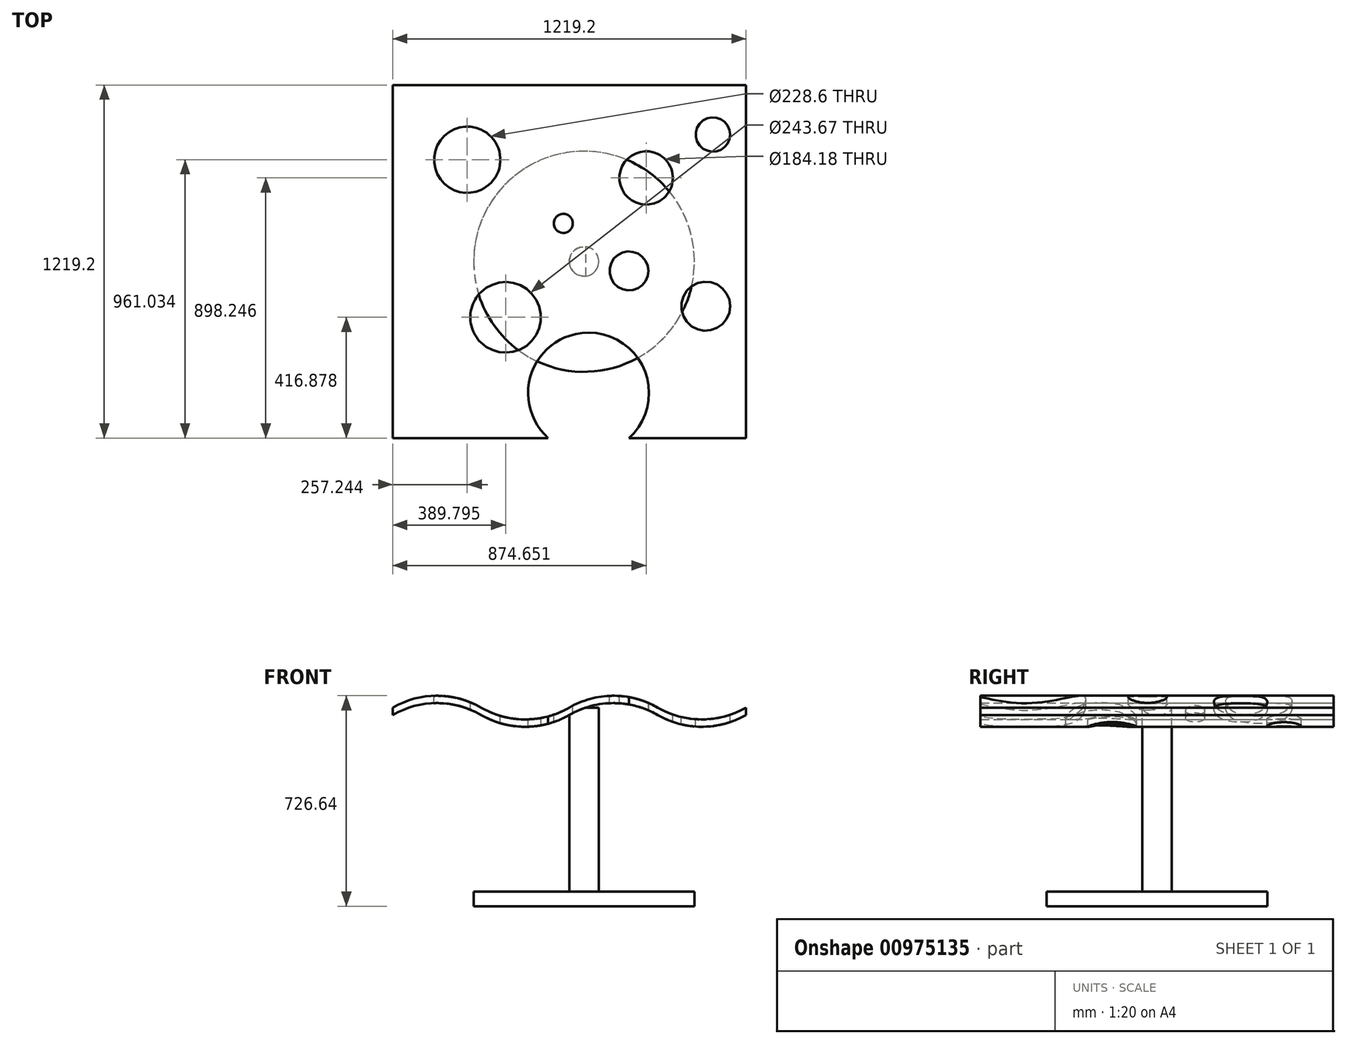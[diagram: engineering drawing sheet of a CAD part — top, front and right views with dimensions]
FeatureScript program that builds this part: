
annotation { "Feature Type Name" : "Feature", "Feature Type Description" : "" }
export const myFeature = defineFeature(function(context is Context, id is Id, definition is map)
    precondition{}
    {
        {
            var Q0;
            Q0=qCreatedBy(makeId("Front.planeOp"),FACE);
            var sketch = newSketch(context, id + "F0", { "sketchPlane" : qUnion([Q0])});
            skArc(sketch, "E0", {"start": v(-355.6, 0) * mm, "mid": v(-508, 40.84) * mm, "end": v(-660.4, 0) * mm});
            skArc(sketch, "E1", {"start": v(-355.6, 0) * mm, "mid": v(-203.2, -40.84) * mm, "end": v(-50.8, 0) * mm});
            skArc(sketch, "E2", {"start": v(254, 0) * mm, "mid": v(101.6, 40.84) * mm, "end": v(-50.8, 0) * mm});
            skArc(sketch, "E3", {"start": v(254, 0) * mm, "mid": v(406.4, -40.84) * mm, "end": v(558.8, 0) * mm});
            skLineSegment(sketch, "E4", {"start": v(-660.4, 0) * mm, "end": v(-660.4, -25.4) * mm});
            skLineSegment(sketch, "E5", {"start": v(-355.6, 0) * mm, "end": v(-355.6, -25.4) * mm});
            skLineSegment(sketch, "E6", {"start": v(-50.8, 0) * mm, "end": v(-50.8, -25.4) * mm});
            skLineSegment(sketch, "E7", {"start": v(254, 0) * mm, "end": v(254, -25.4) * mm});
            skLineSegment(sketch, "E8", {"start": v(558.8, 0) * mm, "end": v(558.8, -25.4) * mm});
            skArc(sketch, "E9", {"start": v(-355.6, -25.4) * mm, "mid": v(-508, 15.44) * mm, "end": v(-660.4, -25.4) * mm});
            skArc(sketch, "E10", {"start": v(-355.6, -25.4) * mm, "mid": v(-203.2, -66.24) * mm, "end": v(-50.8, -25.4) * mm});
            skArc(sketch, "E11", {"start": v(254, -25.4) * mm, "mid": v(101.6, 15.44) * mm, "end": v(-50.8, -25.4) * mm});
            skArc(sketch, "E12", {"start": v(254, -25.4) * mm, "mid": v(406.4, -66.24) * mm, "end": v(558.8, -25.4) * mm});
            skSolve(sketch);
        }
        {
            var Q0;
            Q0=makeQuery(id+"F0.imprint","IMPRINT",FACE,{"disambiguationData":[TD([[makeQuery(id+"F0.imprint","IMPRINT",EDGE,{"derivedFrom":sQuery(id+"F0.wireOp",EDGE,"E0")}),1.0]])]});
            var Q1;
            Q1=makeQuery(id+"F0.imprint","IMPRINT",FACE,{"disambiguationData":[TD([[makeQuery(id+"F0.imprint","IMPRINT",EDGE,{"derivedFrom":sQuery(id+"F0.wireOp",EDGE,"E1")}),-1.0]])]});
            var Q2;
            Q2=makeQuery(id+"F0.imprint","IMPRINT",FACE,{"disambiguationData":[TD([[makeQuery(id+"F0.imprint","IMPRINT",EDGE,{"derivedFrom":sQuery(id+"F0.wireOp",EDGE,"E2")}),1.0]])]});
            var Q3;
            Q3=makeQuery(id+"F0.imprint","IMPRINT",FACE,{"disambiguationData":[TD([[makeQuery(id+"F0.imprint","IMPRINT",EDGE,{"derivedFrom":sQuery(id+"F0.wireOp",EDGE,"E3")}),-1.0]])]});
            extrude(context, id + "F1", {"entities" : qUnion([Q0, Q1, Q2, Q3]), "endBound" : BoundingType.SYMMETRIC, "depth" : 1219.2 * mm, "offsetDistance" : 25.4 * mm});
        }
        {
            var Q0;
            Q0=qCreatedBy(makeId("Top.planeOp"),FACE);
            var sketch = newSketch(context, id + "F2", { "sketchPlane" : qUnion([Q0])});
            skCircle(sketch, "E13", {"center": v(-403.16, 351.43) * mm, "radius": 114.3 * mm});
            skCircle(sketch, "E14", {"center": v(214.25, 288.65) * mm, "radius": 92.1 * mm});
            skCircle(sketch, "E15", {"center": v(-270.6, -192.72) * mm, "radius": 121.84 * mm});
            skCircle(sketch, "E16", {"center": v(-71.78, 131.68) * mm, "radius": 32.9 * mm});
            skCircle(sketch, "E17", {"center": v(420.05, -154.35) * mm, "radius": 84.44 * mm});
            skCircle(sketch, "E18", {"center": v(444.47, 438.64) * mm, "radius": 59.4 * mm});
            skCircle(sketch, "E19", {"center": v(154.95, -32.27) * mm, "radius": 67 * mm});
            skCircle(sketch, "E20", {"center": v(15.42, -454.33) * mm, "radius": 208.65 * mm});
            skSolve(sketch);
        }
        {
            var Q0;
            Q0 = qSketchRegion(id + "F2", true);
            extrude(context, id + "F3", {"entities" : qUnion([Q0]), "operationType" : NewBodyOperationType.REMOVE, "endBound" : BoundingType.SYMMETRIC, "oppositeDirection" : true, "depth" : 254 * mm, "offsetDistance" : 25.4 * mm});
        }
        {
            var Q0;
            Q0=qCreatedBy(makeId("Top.planeOp"),FACE);
            var sketch = newSketch(context, id + "F4", { "sketchPlane" : qUnion([Q0])});
            skCircle(sketch, "E21", {"center": v(0, 0) * mm, "radius": 50.8 * mm});
            skSolve(sketch);
        }
        {
            var Q0;
            Q0 = qSketchRegion(id + "F4", true);
            extrude(context, id + "F5", {"entities" : qUnion([Q0]), "operationType" : NewBodyOperationType.ADD, "oppositeDirection" : true, "depth" : 635 * mm, "offsetDistance" : 25.4 * mm});
        }
        {
            var Q0;
            Q0=makeQuery(id+"F5.opExtrude","CAP_FACE",FACE,{"disambiguationData":[OSD([sQuery(id+"F4.wireOp",EDGE,"E21")])],"isStart":false});
            var sketch = newSketch(context, id + "F6", { "sketchPlane" : qUnion([Q0])});
            skCircle(sketch, "E22", {"center": v(0, 0) * mm, "radius": 381 * mm});
            skSolve(sketch);
        }
        {
            var Q0;
            Q0=makeQuery(id+"F6.imprint","IMPRINT",FACE,{"disambiguationData":[TD([[makeQuery(id+"F6.imprint","IMPRINT",EDGE,{"derivedFrom":sQuery(id+"F6.wireOp",EDGE,"E22")}),1.0]])]});
            var Q1;
            Q1=makeQuery(id+"F6.imprint","IMPRINT",FACE,{"disambiguationData":[TD([[makeQuery(id+"F6.imprint","IMPRINT",EDGE,{"derivedFrom":makeQuery(id+"F5.opExtrude","CAP_EDGE",EDGE,{"disambiguationData":[OSD([sQuery(id+"F4.wireOp",EDGE,"E21")])],"isStart":false})}),-1.0]])]});
            extrude(context, id + "F7", {"entities" : qUnion([Q0, Q1]), "operationType" : NewBodyOperationType.ADD, "depth" : 50.8 * mm, "offsetDistance" : 25.4 * mm});
        }
    });
